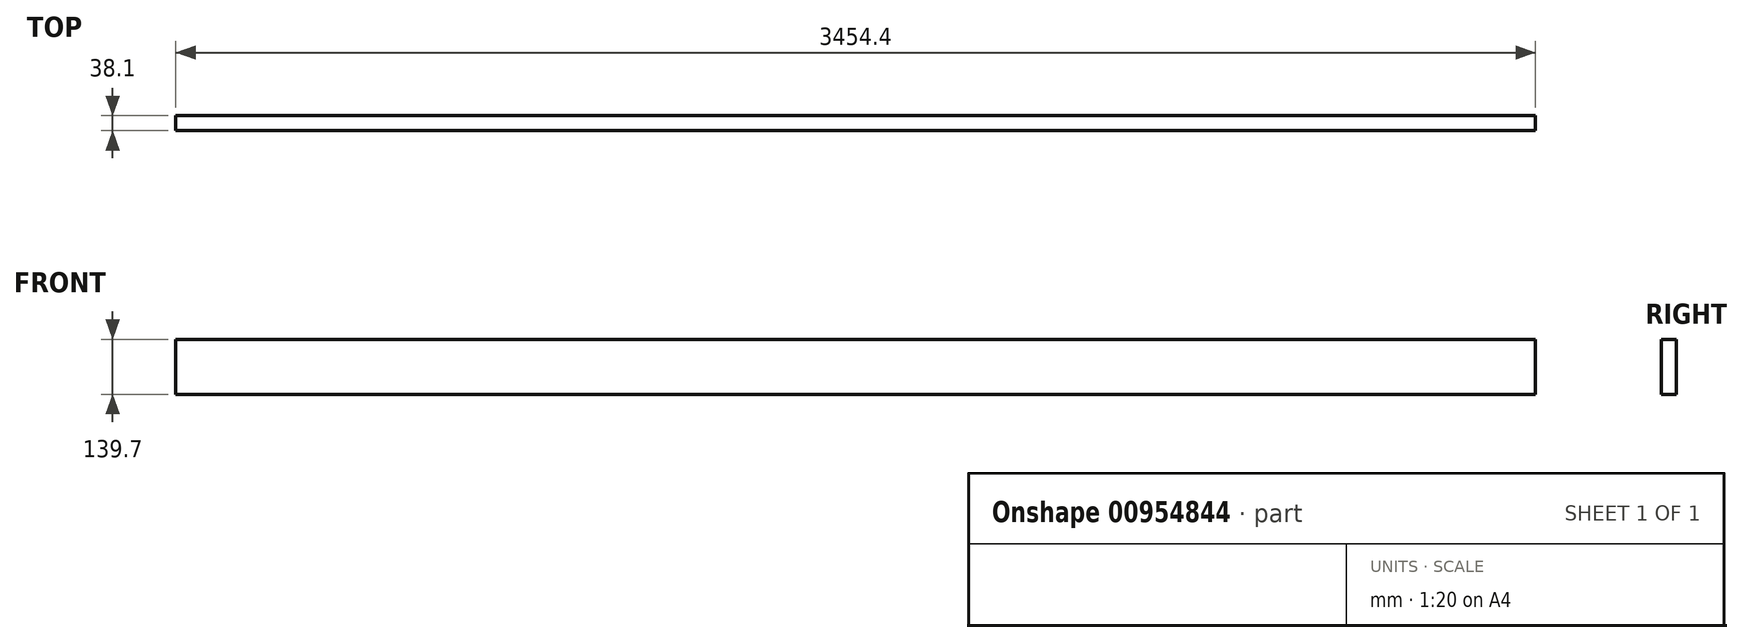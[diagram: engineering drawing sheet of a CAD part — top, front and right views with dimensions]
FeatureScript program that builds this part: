
annotation { "Feature Type Name" : "Feature", "Feature Type Description" : "" }
export const myFeature = defineFeature(function(context is Context, id is Id, definition is map)
    precondition{}
    {
        {
            var Q0;
            Q0=qCreatedBy(makeId("Right.planeOp"),FACE);
            var sketch = newSketch(context, id + "F0", { "sketchPlane" : qUnion([Q0])});
            skLineSegment(sketch, "E0.bottom", {"start": v(-19.05, 69.85) * mm, "end": v(19.05, 69.85) * mm});
            skLineSegment(sketch, "E0.top", {"start": v(-19.05, -69.85) * mm, "end": v(19.05, -69.85) * mm});
            skLineSegment(sketch, "E0.left", {"start": v(-19.05, 69.85) * mm, "end": v(-19.05, -69.85) * mm});
            skLineSegment(sketch, "E0.right", {"start": v(19.05, 69.85) * mm, "end": v(19.05, -69.85) * mm});
            skPoint(sketch, "E1", {"position": v(0, 69.85) * mm});
            skPoint(sketch, "E2", {"position": v(-19.05, 0) * mm});
            skSolve(sketch);
        }
        {
            var Q0;
            Q0=qSketchRegion(id+"F0",true);
            extrude(context, id + "F1", {"entities" : qUnion([Q0]), "endBound" : BoundingType.SYMMETRIC, "depth" : 3454.4 * mm, "offsetDistance" : 25.4 * mm, "hasSecondDirection" : true, "secondDirectionOppositeDirection" : true, "secondDirectionDepth" : 609.6 * mm});
        }
    });
